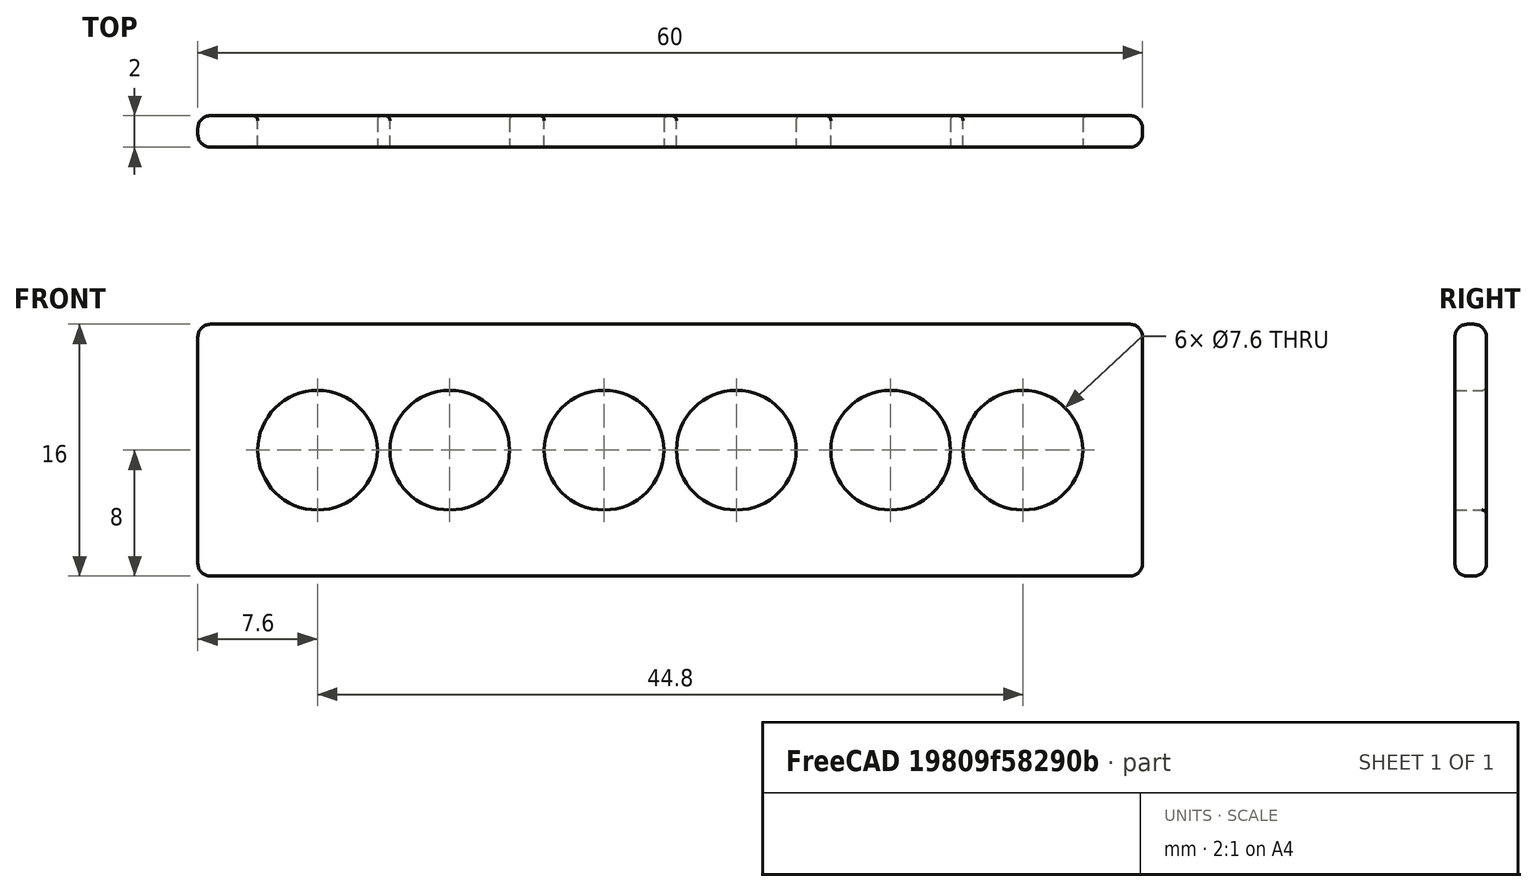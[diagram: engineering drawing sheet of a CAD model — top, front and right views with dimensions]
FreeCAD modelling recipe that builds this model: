
FCSTD DOCUMENT  (FreeCAD 0.16R6712 (Git))
Label: box
License: All rights reserved
LicenseURL: http://en.wikipedia.org/wiki/All_rights_reserved
objects: Sketcher::SketchObject×3, PartDesign::Fillet×2, PartDesign::Pad×1, PartDesign::Pocket×1, Mesh::Feature×1
note: 9 computed .brp shape members not serialized (recipe doc carries the construction recipe); baked Part::Feature solids carry a one-line shape summary decoded from their .brp

FEATURE [Sketcher::SketchObject] Sketch
  Placement = pos=(0,0,0) rot=(-1,0,0;4.71239rad)
FEATURE [Sketcher::SketchObject] Sketch001
  Placement = pos=(0,-3,0) rot=(1,0,0;1.5708rad)
  sketch-geometry (4):
    g0: LineSegment StartX=-30 StartY=8 StartZ=0 EndX=30 EndY=8 EndZ=0
    g1: LineSegment StartX=30 StartY=8 StartZ=0 EndX=30 EndY=-8 EndZ=0
    g2: LineSegment StartX=30 StartY=-8 StartZ=0 EndX=-30 EndY=-8 EndZ=0
    g3: LineSegment StartX=-30 StartY=-8 StartZ=0 EndX=-30 EndY=8 EndZ=0
  constraints (12):
    c: Coincident(g0,g1)
    c: Coincident(g1,g2)
    c: Coincident(g2,g3)
    c: Coincident(g3,g0)
    c: Horizontal(g0)
    c: Horizontal(g2)
    c: Vertical(g1)
    c: Vertical(g3)
    c: Symmetric(g0,g0,g-2)
    c: Symmetric(g1,g0,g-1)
    c: DistanceX(g-2,g0) = 30
    c: DistanceY(g-1,g0) = 8
FEATURE [PartDesign::Pad] Pad
  Length = 2
  Length2 = 100
  Placement = pos=(0,-3,0) rot=(1,0,0;1.5708rad)
  Sketch = -> Sketch001
  Type = 0
FEATURE [PartDesign::Fillet] Fillet
  Base = -> Pad [Edge4,Edge7,Edge10,Edge12,Edge5,Edge8,Edge9,Edge1,Edge11,Edge3,Edge6,Edge2]
  Placement = pos=(0,-3,0) rot=(1,0,0;1.5708rad)
  Radius = 0.8
FEATURE [Sketcher::SketchObject] Sketch002
  Placement = pos=(0,-3,0) rot=(-1,0,0;1.5708rad)
  Support = -> Fillet [Face13]
  sketch-geometry (6):
    g0: Circle CenterX=4.2 CenterY=0 CenterZ=0 NormalX=0 NormalY=0 NormalZ=1 Radius=3.8
    g1: Circle CenterX=-4.2 CenterY=0 CenterZ=0 NormalX=0 NormalY=0 NormalZ=1 Radius=3.8
    g2: Circle CenterX=-14 CenterY=0 CenterZ=0 NormalX=0 NormalY=0 NormalZ=1 Radius=3.8
    g3: Circle CenterX=-22.4 CenterY=0 CenterZ=0 NormalX=0 NormalY=0 NormalZ=1 Radius=3.8
    g4: Circle CenterX=14 CenterY=0 CenterZ=0 NormalX=0 NormalY=0 NormalZ=1 Radius=3.8
    g5: Circle CenterX=22.4 CenterY=0 CenterZ=0 NormalX=0 NormalY=0 NormalZ=1 Radius=3.8
  constraints (18):
    c: PointOnObject(g0,g-1)
    c: Radius(g5) = 3.8
    c: Equal(g5,g4)
    c: Equal(g4,g0)
    c: Equal(g0,g1)
    c: Equal(g1,g2)
    c: Equal(g2,g3)
    c: PointOnObject(g3,g-1)
    c: PointOnObject(g2,g-1)
    c: PointOnObject(g1,g-1)
    c: PointOnObject(g4,g-1)
    c: PointOnObject(g5,g-1)
    c: DistanceX(g-2,g0) = 4.2
    c: DistanceX(g-2,g4) = 14
    c: Distance(g4,g5) = 8.4
    c: Symmetric(g1,g0,g-2)
    c: Symmetric(g2,g4,g-2)
    c: Symmetric(g3,g5,g-2)
FEATURE [PartDesign::Pocket] Pocket
  Length = 5
  Placement = pos=(0,-3,0) rot=(1,0,0;1.5708rad)
  Sketch = -> Sketch002
  Type = 0
FEATURE [PartDesign::Fillet] Fillet001
  Base = -> Pocket [Edge46,Edge47,Edge45,Edge44,Edge43,Edge48]
  Placement = pos=(0,-3,0) rot=(1,0,0;1.5708rad)
  Radius = 0.3
FEATURE [Mesh::Feature] Mesh  label="Fillet001 (Meshed)"
